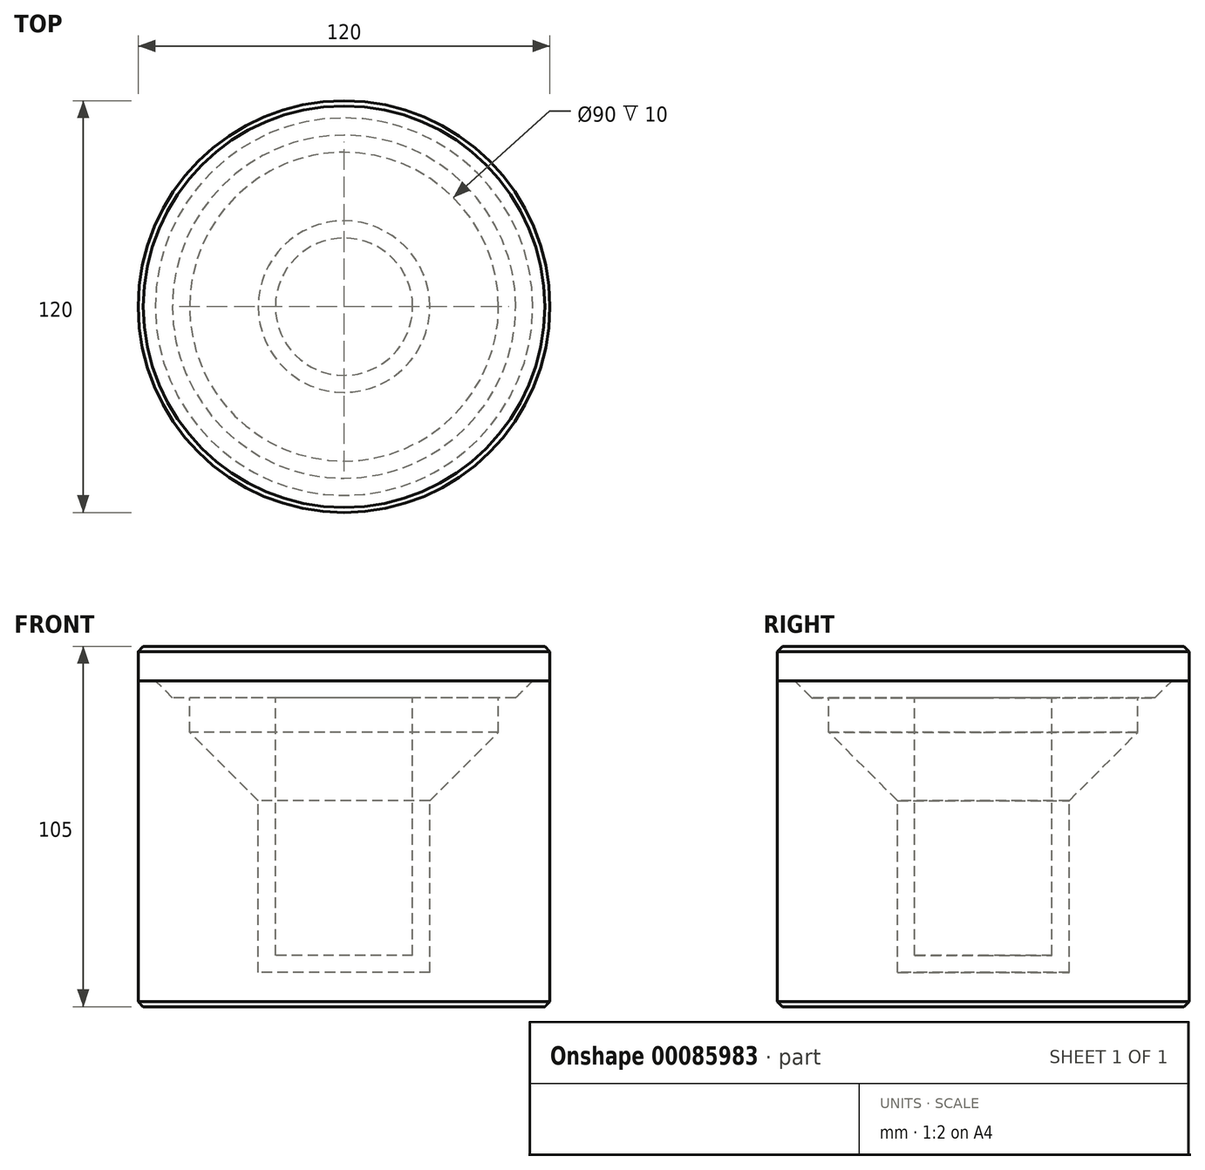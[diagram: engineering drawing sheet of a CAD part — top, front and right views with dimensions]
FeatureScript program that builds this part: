
annotation { "Feature Type Name" : "Feature", "Feature Type Description" : "" }
export const myFeature = defineFeature(function(context is Context, id is Id, definition is map)
    precondition{}
    {
        {
            var Q0;
            Q0=qCreatedBy(makeId("Front.planeOp"),FACE);
            var sketch = newSketch(context, id + "F0", { "sketchPlane" : qUnion([Q0])});
            skLineSegment(sketch, "E0.bottom", {"start": v(60, 45) * mm, "end": v(-60, 45) * mm});
            skLineSegment(sketch, "E0.top", {"start": v(60, -45) * mm, "end": v(-60, -45) * mm});
            skLineSegment(sketch, "E0.left", {"start": v(60, 45) * mm, "end": v(60, -45) * mm});
            skLineSegment(sketch, "E0.right", {"start": v(-60, 45) * mm, "end": v(-60, -45) * mm});
            skPoint(sketch, "E0.middle", {"position": v(0, 0) * mm});
            skLineSegment(sketch, "E1", {"start": v(0, 121.28) * mm, "end": v(0, -93.9) * mm});
            skLineSegment(sketch, "E2.top", {"start": v(25, -35) * mm, "end": v(-25, -35) * mm});
            skLineSegment(sketch, "E2.left", {"start": v(25, 35) * mm, "end": v(25, -35) * mm});
            skLineSegment(sketch, "E2.right", {"start": v(-25, 35) * mm, "end": v(-25, -35) * mm});
            skLineSegment(sketch, "E3", {"start": v(-25, 35) * mm, "end": v(-25, 45) * mm});
            skLineSegment(sketch, "E4", {"start": v(25, 30.56) * mm, "end": v(25, 45) * mm});
            skLineSegment(sketch, "E5", {"start": v(-60, 35) * mm, "end": v(60, 35) * mm});
            skLineSegment(sketch, "E6", {"start": v(-45, 45) * mm, "end": v(-45, 35) * mm});
            skLineSegment(sketch, "E7", {"start": v(45, 45) * mm, "end": v(45, 35) * mm});
            skLineSegment(sketch, "E8.top", {"start": v(20, -30) * mm, "end": v(-20, -30) * mm});
            skLineSegment(sketch, "E8.left", {"start": v(20, 30) * mm, "end": v(20, -30) * mm});
            skLineSegment(sketch, "E8.right", {"start": v(-20, 30) * mm, "end": v(-20, -30) * mm});
            skLineSegment(sketch, "E9", {"start": v(-20, 30) * mm, "end": v(-20, 45) * mm});
            skLineSegment(sketch, "E10", {"start": v(20, 30) * mm, "end": v(20, 45) * mm});
            skLineSegment(sketch, "E11", {"start": v(-60, 45) * mm, "end": v(-60, 60) * mm});
            skLineSegment(sketch, "E12", {"start": v(-60, 60) * mm, "end": v(60, 60) * mm});
            skLineSegment(sketch, "E13", {"start": v(60, 60) * mm, "end": v(60, 45) * mm});
            skPoint(sketch, "E14.orphan", {"position": v(0, 65.26) * mm});
            skLineSegment(sketch, "E15", {"start": v(-45, 35) * mm, "end": v(-25, 15) * mm});
            skPoint(sketch, "E16", {"position": v(-25, 40) * mm});
            skPoint(sketch, "E17.end.orphan", {"position": v(-46.37, 45) * mm});
            skPoint(sketch, "E18.end.orphan", {"position": v(-60, 56) * mm});
            skPoint(sketch, "E19.MirrorCS.end.orphan", {"position": v(46.37, 45) * mm});
            skPoint(sketch, "E20.MirrorCS.end.orphan", {"position": v(60, 56) * mm});
            skLineSegment(sketch, "E21", {"start": v(-60, 50) * mm, "end": v(-55, 50) * mm});
            skLineSegment(sketch, "E22", {"start": v(-55, 50) * mm, "end": v(-50, 45) * mm});
            skSolve(sketch);
        }
        {
            var Q0;
            {var subQ4=sQuery(id+"F0.wireOp",EDGE,"E18");Q0=makeQuery(id+"F0.imprint","IMPRINT",FACE,{"disambiguationData":[TD([[makeQuery(id+"F0.imprint","IMPRINT",EDGE,{"derivedFrom":subQ4}),1.0]])]});}
            var Q1;
            {var subQ3=sQuery(id+"F0.wireOp",EDGE,"E6");Q1=makeQuery(id+"F0.imprint","IMPRINT",FACE,{"disambiguationData":[TD([[makeQuery(id+"F0.imprint","IMPRINT",EDGE,{"derivedFrom":subQ3}),-1.0]])]});}
            var Q2;
            {var subQ10=sQuery(id+"F0.wireOp",EDGE,"E15");Q2=makeQuery(id+"F0.imprint","IMPRINT",FACE,{"disambiguationData":[TD([[makeQuery(id+"F0.imprint","IMPRINT",EDGE,{"derivedFrom":subQ10}),-1.0]])]});}
            var Q3;
            {var subQ4=sQuery(id+"F0.wireOp",EDGE,"E21");Q3=makeQuery(id+"F0.imprint","IMPRINT",FACE,{"disambiguationData":[TD([[makeQuery(id+"F0.imprint","IMPRINT",EDGE,{"derivedFrom":subQ4}),-1.0]])]});}
            var Q4;
            Q4=sQuery(id+"F0.wireOp",EDGE,"E1");
            revolve(context, id + "F1", {"entities" : qUnion([Q0, Q1, Q2, Q3]), "axis" : qUnion([Q4]), "revolveType" : RevolveType.FULL});
        }
        {
            var Q0;
            {var subQ9=sQuery(id+"F0.wireOp",EDGE,"E18");Q0=makeQuery(id+"F0.imprint","IMPRINT",FACE,{"disambiguationData":[TD([[makeQuery(id+"F0.imprint","IMPRINT",EDGE,{"derivedFrom":subQ9}),-1.0]])]});}
            var Q1;
            {var subQ0=sQuery(id+"F0.wireOp",EDGE,"E8.right");Q1=makeQuery(id+"F0.imprint","IMPRINT",FACE,{"disambiguationData":[TD([[makeQuery(id+"F0.imprint","IMPRINT",EDGE,{"derivedFrom":subQ0}),1.0]])]});}
            var Q2;
            {var subQ0=sQuery(id+"F0.wireOp",EDGE,"E9");var subQ1=sQuery(id+"F0.wireOp",EDGE,"E0.bottom");var subQ2=makeQuery(id+"F0.imprint","INTERSECT",VERTEX,{"derivedFrom":[subQ1,subQ0]});Q2=makeQuery(id+"F0.imprint","IMPRINT",FACE,{"disambiguationData":[TD([[makeQuery(id+"F0.imprint","IMPRINT",EDGE,{"disambiguationData":[TD([[subQ2,1.0]])],"derivedFrom":subQ1}),1.0]])]});}
            var Q3;
            {var subQ11=sQuery(id+"F0.wireOp",EDGE,"E21");Q3=makeQuery(id+"F0.imprint","IMPRINT",FACE,{"disambiguationData":[TD([[makeQuery(id+"F0.imprint","IMPRINT",EDGE,{"derivedFrom":subQ11}),1.0]])]});}
            var Q4;
            Q4=sQuery(id+"F0.wireOp",EDGE,"E1");
            revolve(context, id + "F2", {"entities" : qUnion([Q0, Q1, Q2, Q3]), "axis" : qUnion([Q4]), "revolveType" : RevolveType.FULL});
        }
        {
            var Q0;
            {var subQ3=sQuery(id+"F0.wireOp",EDGE,"E6");Q0=makeQuery(id+"F0.imprint","IMPRINT",FACE,{"disambiguationData":[TD([[makeQuery(id+"F0.imprint","IMPRINT",EDGE,{"derivedFrom":subQ3}),1.0]])]});}
            var Q1;
            {var subQ0=sQuery(id+"F0.wireOp",EDGE,"E3");var subQ1=sQuery(id+"F0.wireOp",EDGE,"E0.bottom");var subQ2=makeQuery(id+"F0.imprint","INTERSECT",VERTEX,{"derivedFrom":[subQ1,subQ0]});Q1=makeQuery(id+"F0.imprint","IMPRINT",FACE,{"disambiguationData":[TD([[makeQuery(id+"F0.imprint","IMPRINT",EDGE,{"disambiguationData":[TD([[subQ2,1.0]])],"derivedFrom":subQ1}),1.0]])]});}
            var Q2;
            {var subQ1=sQuery(id+"F0.wireOp",EDGE,"E2.right");Q2=makeQuery(id+"F0.imprint","IMPRINT",FACE,{"disambiguationData":[TD([[makeQuery(id+"F0.imprint","IMPRINT",EDGE,{"derivedFrom":subQ1}),1.0]])]});}
            var Q3;
            {var subQ3=sQuery(id+"F0.wireOp",EDGE,"E15");Q3=makeQuery(id+"F0.imprint","IMPRINT",FACE,{"disambiguationData":[TD([[makeQuery(id+"F0.imprint","IMPRINT",EDGE,{"derivedFrom":subQ3}),1.0]])]});}
            var Q4;
            Q4=sQuery(id+"F0.wireOp",EDGE,"E1");
            revolve(context, id + "F3", {"entities" : qUnion([Q0, Q1, Q2, Q3]), "axis" : qUnion([Q4]), "revolveType" : RevolveType.FULL});
        }
        {
            var Q0;
            Q0=makeQuery(id+"F2.opRevolve","SWEPT_EDGE",EDGE,{"disambiguationData":[OSD([sQuery(id+"F0.wireOp",EDGE,"E11"),sQuery(id+"F0.wireOp",EDGE,"E12")])]});
            chamfer(context, id + "F4", {"entities" : qUnion([Q0]), "width" : 1.5 * mm, "tangentPropagation" : true});
        }
        {
            var Q0;
            Q0=makeQuery(id+"F1.opRevolve","SWEPT_EDGE",EDGE,{"disambiguationData":[OSD([sQuery(id+"F0.wireOp",EDGE,"E0.top"),sQuery(id+"F0.wireOp",EDGE,"E0.right")])]});
            chamfer(context, id + "F5", {"entities" : qUnion([Q0]), "width" : 1.5 * mm, "tangentPropagation" : true});
        }
    });
